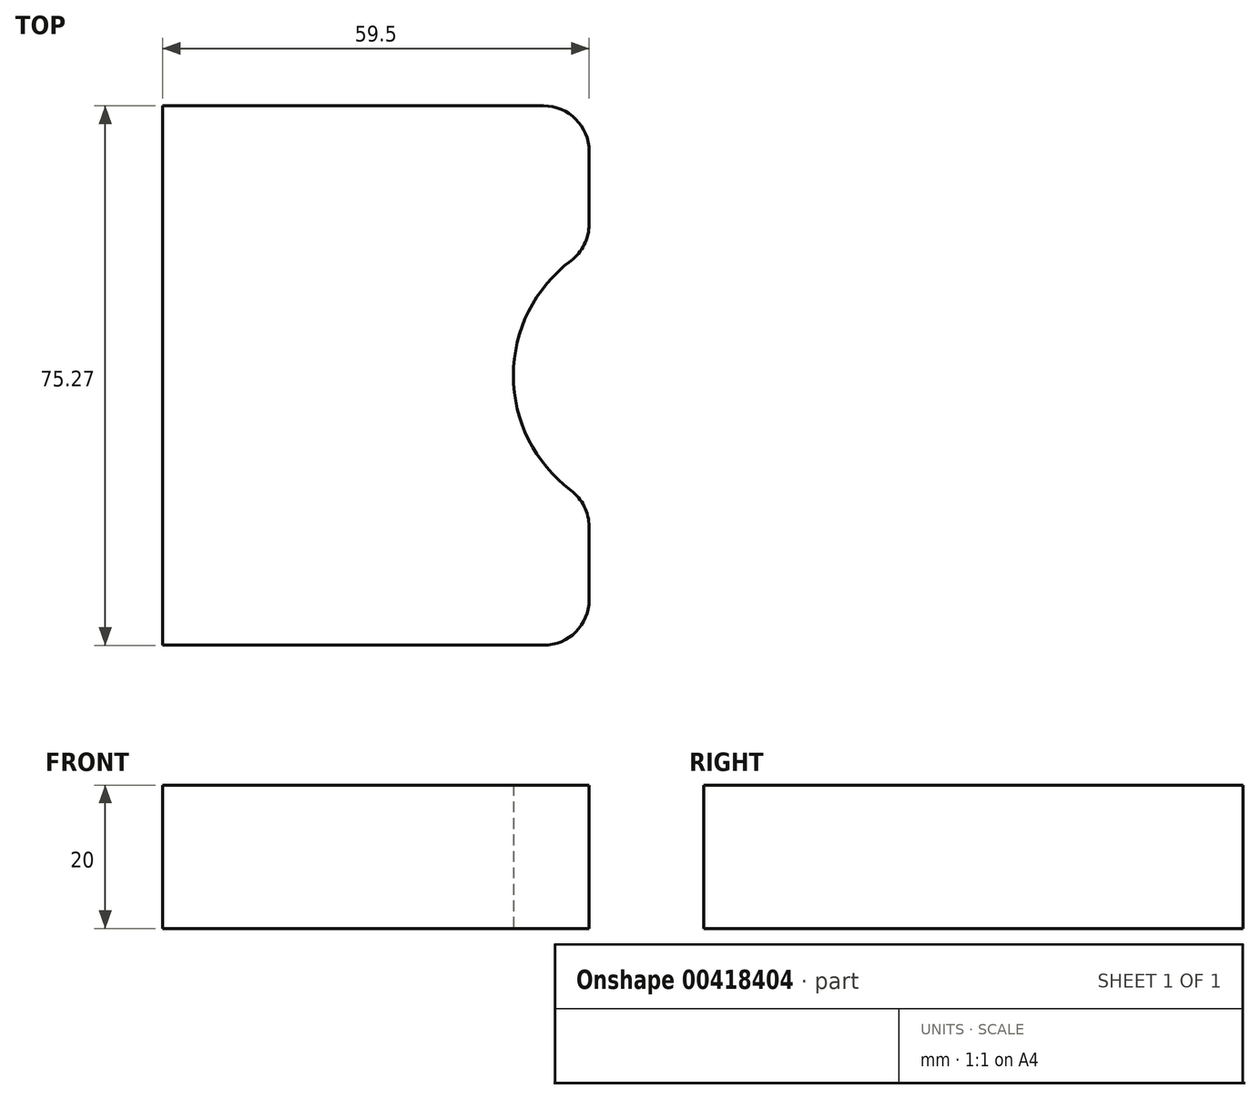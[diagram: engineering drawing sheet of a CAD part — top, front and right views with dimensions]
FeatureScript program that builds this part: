
annotation { "Feature Type Name" : "Feature", "Feature Type Description" : "" }
export const myFeature = defineFeature(function(context is Context, id is Id, definition is map)
    precondition{}
    {
        {
            var Q0;
            Q0=qCreatedBy(makeId("Top.planeOp"),FACE);
            var sketch = newSketch(context, id + "F0", { "sketchPlane" : qUnion([Q0])});
            skLineSegment(sketch, "E0", {"start": v(-27.95, -34.89) * mm, "end": v(-27.95, 40.38) * mm});
            skLineSegment(sketch, "E1", {"start": v(-27.95, 40.38) * mm, "end": v(25.2, 40.38) * mm});
            skLineSegment(sketch, "E2", {"start": v(25.2, -34.89) * mm, "end": v(-27.95, -34.89) * mm});
            skLineSegment(sketch, "E3", {"start": v(31.55, 34.03) * mm, "end": v(31.55, 23.84) * mm});
            skLineSegment(sketch, "E4", {"start": v(31.55, -18.35) * mm, "end": v(31.55, -28.54) * mm});
            skArc(sketch, "E5", {"start": v(29, 18.76) * mm, "mid": v(21, 2.75) * mm, "end": v(29, -13.27) * mm});
            skPoint(sketch, "E6.visualSharp", {"position": v(31.55, 40.38) * mm});
            skArc(sketch, "E6.filletArc", {"start": v(31.55, 34.03) * mm, "mid": v(29.7, 38.52) * mm, "end": v(25.2, 40.38) * mm});
            skPoint(sketch, "E7.visualSharp", {"position": v(31.55, -34.89) * mm});
            skArc(sketch, "E7.filletArc", {"start": v(25.2, -34.89) * mm, "mid": v(29.7, -33.03) * mm, "end": v(31.55, -28.54) * mm});
            skPoint(sketch, "E8.visualSharp", {"position": v(31.55, -14.89) * mm});
            skArc(sketch, "E8.filletArc", {"start": v(31.55, -18.35) * mm, "mid": v(30.88, -15.5) * mm, "end": v(29, -13.27) * mm});
            skPoint(sketch, "E9.visualSharp", {"position": v(31.55, 20.38) * mm});
            skArc(sketch, "E9.filletArc", {"start": v(29, 18.76) * mm, "mid": v(30.88, 21) * mm, "end": v(31.55, 23.84) * mm});
            skSolve(sketch);
        }
        {
            var Q0;
            Q0=makeQuery(id+"F0.imprint","IMPRINT",FACE,{"disambiguationData":[TD([[makeQuery(id+"F0.imprint","IMPRINT",EDGE,{"derivedFrom":sQuery(id+"F0.wireOp",EDGE,"E0")}),-1.0]])]});
            var Q1;
            Q1=makeQuery(id+"F0.imprint","IMPRINT",FACE,{"disambiguationData":[TD([[makeQuery(id+"F0.imprint","IMPRINT",EDGE,{"derivedFrom":sQuery(id+"F0.wireOp",EDGE,"E0")}),-1.0]])]});
            extrude(context, id + "F1", {"entities" : qUnion([Q0, Q1]), "depth" : 20 * mm});
        }
    });
